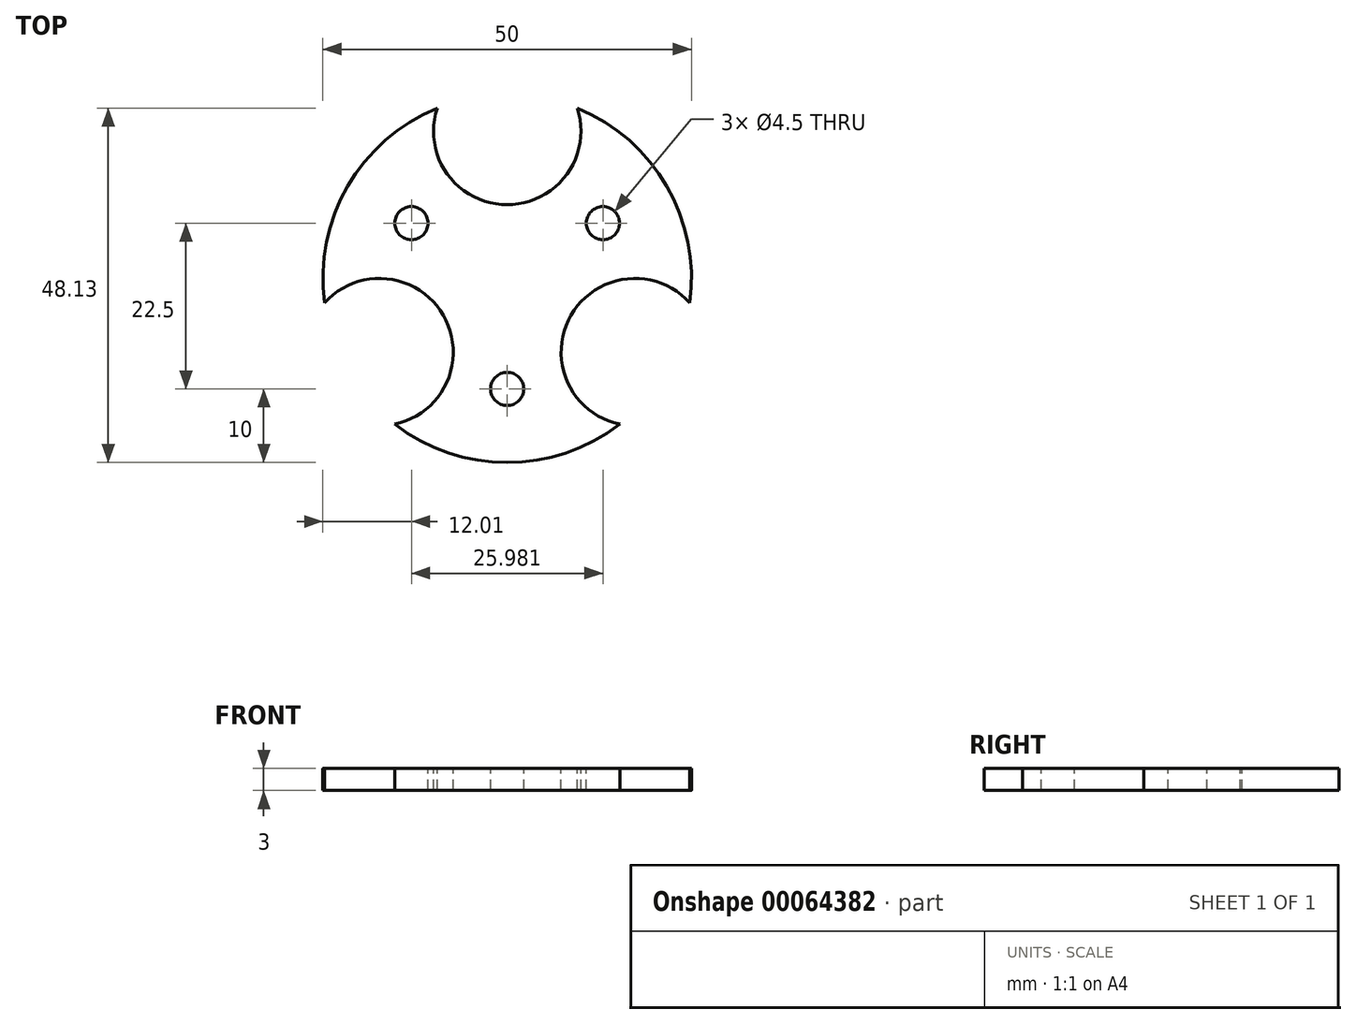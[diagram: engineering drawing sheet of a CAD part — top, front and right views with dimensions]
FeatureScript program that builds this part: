
annotation { "Feature Type Name" : "Feature", "Feature Type Description" : "" }
export const myFeature = defineFeature(function(context is Context, id is Id, definition is map)
    precondition{}
    {
        {
            var Q0;
            Q0=qCreatedBy(makeId("Top.planeOp"),FACE);
            var sketch = newSketch(context, id + "F0", { "sketchPlane" : qUnion([Q0])});
            skCircle(sketch, "E0", {"center": v(0, 0) * mm, "radius": 25 * mm});
            skSolve(sketch);
        }
        {
            var Q0;
            Q0=makeQuery(id+"F0.imprint","IMPRINT",FACE,{"disambiguationData":[TD([[makeQuery(id+"F0.imprint","IMPRINT",EDGE,{"derivedFrom":sQuery(id+"F0.wireOp",EDGE,"E0")}),1.0]])]});
            extrude(context, id + "F1", {"entities" : qUnion([Q0]), "depth" : 3 * mm});
        }
        {
            var Q0;
            Q0=makeQuery(id+"F1.opExtrude","CAP_FACE",FACE,{"disambiguationData":[OSD([sQuery(id+"F0.wireOp",EDGE,"E0")])],"isStart":false});
            var sketch = newSketch(context, id + "F2", { "sketchPlane" : qUnion([Q0])});
            skCircle(sketch, "E1", {"center": v(0, 18) * mm, "radius": 10 * mm, "construction": true});
            skCircle(sketch, "E2.1.0", {"center": v(-15.59, -9) * mm, "radius": 10 * mm, "construction": true});
            skCircle(sketch, "E2.2.0", {"center": v(15.59, -9) * mm, "radius": 10 * mm, "construction": true});
            skPoint(sketch, "E2.center", {"position": v(0, 0) * mm});
            skCircle(sketch, "E3", {"center": v(0, 15) * mm, "radius": 2.25 * mm});
            skCircle(sketch, "E4.1.0", {"center": v(-13, 7.5) * mm, "radius": 2.25 * mm});
            skCircle(sketch, "E4.2.0", {"center": v(-13, -7.5) * mm, "radius": 2.25 * mm});
            skCircle(sketch, "E5.1.3.0", {"center": v(0, -15) * mm, "radius": 2.25 * mm});
            skCircle(sketch, "E5.1.4.0", {"center": v(13, -7.5) * mm, "radius": 2.25 * mm});
            skCircle(sketch, "E5.1.5.0", {"center": v(13, 7.5) * mm, "radius": 2.25 * mm});
            skSolve(sketch);
        }
        {
            var Q0;
            Q0 = qSketchRegion(id + "F2", true);
            extrude(context, id + "F3", {"entities" : qUnion([Q0]), "operationType" : NewBodyOperationType.REMOVE, "oppositeDirection" : true, "depth" : 25 * mm});
        }
        {
            var Q0;
            Q0=makeQuery(id+"F1.opExtrude","CAP_FACE",FACE,{"disambiguationData":[OSD([sQuery(id+"F0.wireOp",EDGE,"E0")])],"isStart":false});
            var sketch = newSketch(context, id + "F4", { "sketchPlane" : qUnion([Q0])});
            skCircle(sketch, "E6", {"center": v(0, 20) * mm, "radius": 10 * mm});
            skCircle(sketch, "E7.1.0", {"center": v(-17.32, -10) * mm, "radius": 10 * mm});
            skCircle(sketch, "E7.2.0", {"center": v(17.32, -10) * mm, "radius": 10 * mm});
            skPoint(sketch, "E7.center", {"position": v(0, 0) * mm});
            skSolve(sketch);
        }
        {
            var Q0;
            Q0 = qSketchRegion(id + "F4", true);
            extrude(context, id + "F5", {"entities" : qUnion([Q0]), "operationType" : NewBodyOperationType.REMOVE, "oppositeDirection" : true, "depth" : 25 * mm});
        }
    });
